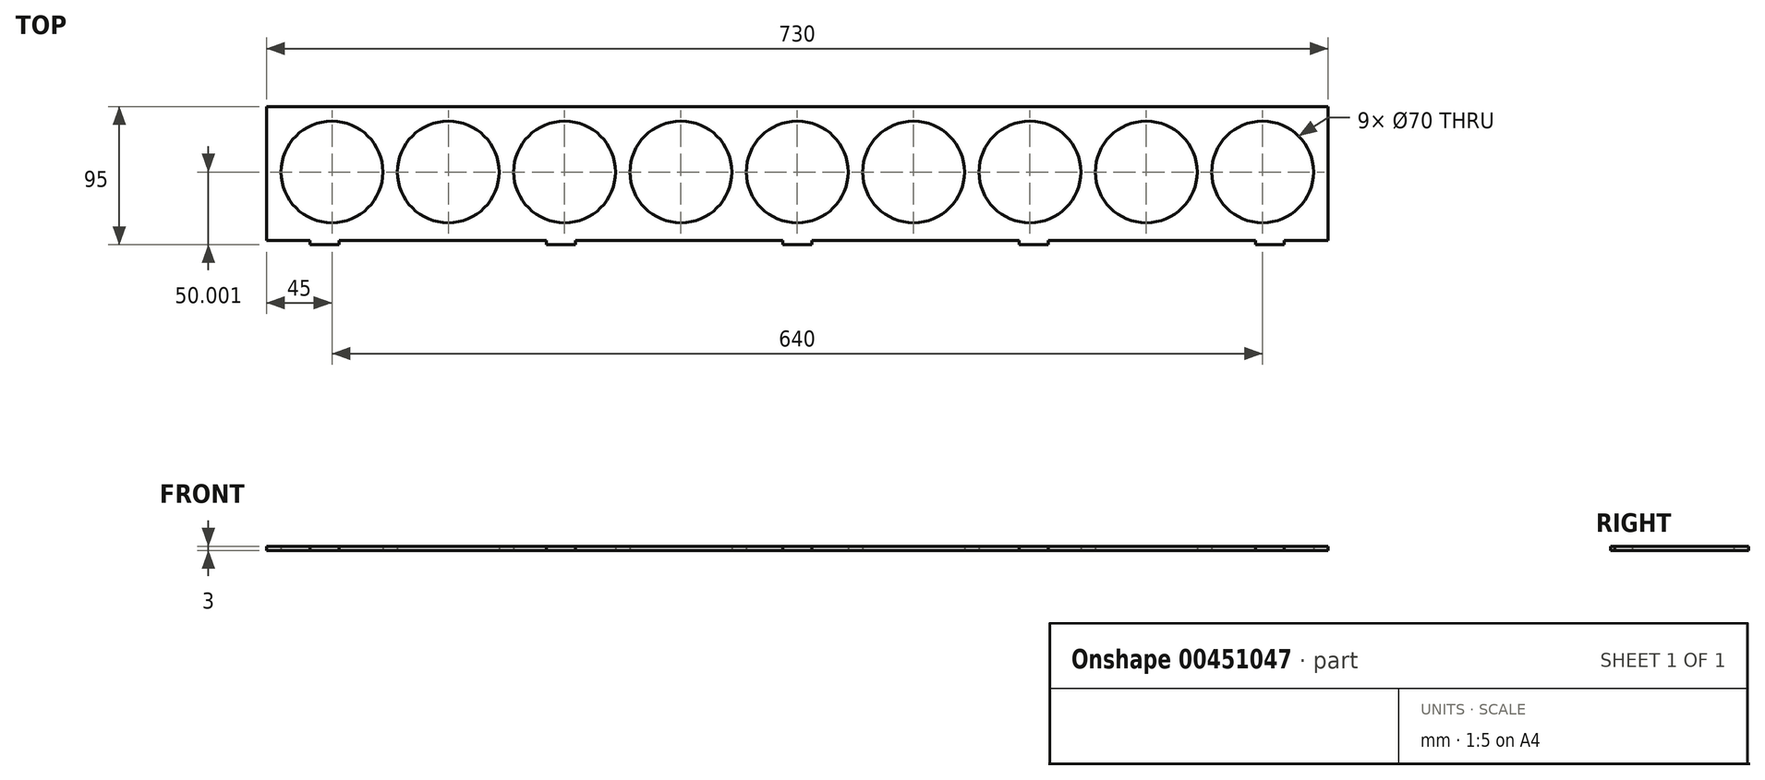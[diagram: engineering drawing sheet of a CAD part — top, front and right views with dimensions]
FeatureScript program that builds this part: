
annotation { "Feature Type Name" : "Feature", "Feature Type Description" : "" }
export const myFeature = defineFeature(function(context is Context, id is Id, definition is map)
    precondition{}
    {
        {
            var Q0;
            Q0=qCreatedBy(makeId("Top.planeOp"),FACE);
            var sketch = newSketch(context, id + "F0", { "sketchPlane" : qUnion([Q0])});
            skLineSegment(sketch, "E0.bottom", {"start": v(-365, 99.13) * mm, "end": v(365, 99.13) * mm});
            skLineSegment(sketch, "E0.left", {"start": v(-365, 99.13) * mm, "end": v(-365, 7.13) * mm});
            skLineSegment(sketch, "E0.right", {"start": v(365, 99.13) * mm, "end": v(365, 7.13) * mm});
            skCircle(sketch, "E1", {"center": v(-320, 54.13) * mm, "radius": 35 * mm});
            skCircle(sketch, "E2.1.0.0", {"center": v(-240, 54.13) * mm, "radius": 35 * mm});
            skCircle(sketch, "E2.2.0.0", {"center": v(-160, 54.13) * mm, "radius": 35 * mm});
            skCircle(sketch, "E2.3.0.0", {"center": v(-80, 54.13) * mm, "radius": 35 * mm});
            skCircle(sketch, "E2.4.0.0", {"center": v(0, 54.13) * mm, "radius": 35 * mm});
            skCircle(sketch, "E2.5.0.0", {"center": v(80, 54.13) * mm, "radius": 35 * mm});
            skCircle(sketch, "E2.6.0.0", {"center": v(160, 54.13) * mm, "radius": 35 * mm});
            skCircle(sketch, "E2.7.0.0", {"center": v(240, 54.13) * mm, "radius": 35 * mm});
            skCircle(sketch, "E2.8.0.0", {"center": v(320, 54.13) * mm, "radius": 35 * mm});
            skLineSegment(sketch, "E2.direction1", {"start": v(-320, 54.13) * mm, "end": v(-240, 54.13) * mm, "construction": true});
            skLineSegment(sketch, "E3", {"start": v(-365, 7.13) * mm, "end": v(-335, 7.13) * mm});
            skLineSegment(sketch, "E4", {"start": v(-335, 7.13) * mm, "end": v(-335, 4.13) * mm});
            skLineSegment(sketch, "E5", {"start": v(-335, 4.13) * mm, "end": v(-325, 4.13) * mm});
            skLineSegment(sketch, "E6.MirrorCS", {"start": v(-315, 4.13) * mm, "end": v(-325, 4.13) * mm});
            skLineSegment(sketch, "E7.MirrorCS", {"start": v(-315, 7.13) * mm, "end": v(-315, 4.13) * mm});
            skLineSegment(sketch, "E8", {"start": v(-162.5, 4.13) * mm, "end": v(-172.5, 4.13) * mm});
            skLineSegment(sketch, "E9", {"start": v(-172.5, 4.13) * mm, "end": v(-172.5, 7.13) * mm});
            skLineSegment(sketch, "E10", {"start": v(0, 4.13) * mm, "end": v(-10, 4.13) * mm});
            skLineSegment(sketch, "E11", {"start": v(-10, 4.13) * mm, "end": v(-10, 7.13) * mm});
            skLineSegment(sketch, "E12", {"start": v(162.5, 4.13) * mm, "end": v(152.5, 4.13) * mm});
            skLineSegment(sketch, "E13", {"start": v(152.5, 4.13) * mm, "end": v(152.5, 7.13) * mm});
            skLineSegment(sketch, "E14", {"start": v(325, 4.13) * mm, "end": v(315, 4.13) * mm});
            skLineSegment(sketch, "E15", {"start": v(315, 4.13) * mm, "end": v(315, 7.13) * mm});
            skLineSegment(sketch, "E16.MirrorCS", {"start": v(-152.5, 4.13) * mm, "end": v(-152.5, 7.13) * mm});
            skLineSegment(sketch, "E17.MirrorCS", {"start": v(-162.5, 4.13) * mm, "end": v(-152.5, 4.13) * mm});
            skLineSegment(sketch, "E18.MirrorCS", {"start": v(10, 4.13) * mm, "end": v(10, 7.13) * mm});
            skLineSegment(sketch, "E19.MirrorCS", {"start": v(0, 4.13) * mm, "end": v(10, 4.13) * mm});
            skLineSegment(sketch, "E20.MirrorCS", {"start": v(325, 4.13) * mm, "end": v(335, 4.13) * mm});
            skLineSegment(sketch, "E21.MirrorCS", {"start": v(335, 4.13) * mm, "end": v(335, 7.13) * mm});
            skLineSegment(sketch, "E22.MirrorCS", {"start": v(162.5, 4.13) * mm, "end": v(172.5, 4.13) * mm});
            skLineSegment(sketch, "E23.MirrorCS", {"start": v(172.5, 4.13) * mm, "end": v(172.5, 7.13) * mm});
            skLineSegment(sketch, "E24.trimOffspring", {"start": v(-315, 7.13) * mm, "end": v(-172.5, 7.13) * mm});
            skLineSegment(sketch, "E25.trimOffspring", {"start": v(-152.5, 7.13) * mm, "end": v(-10, 7.13) * mm});
            skLineSegment(sketch, "E26.trimOffspring", {"start": v(10, 7.13) * mm, "end": v(152.5, 7.13) * mm});
            skLineSegment(sketch, "E27.trimOffspring", {"start": v(335, 7.13) * mm, "end": v(365, 7.13) * mm});
            skLineSegment(sketch, "E28.trimOffspring", {"start": v(172.5, 7.13) * mm, "end": v(315, 7.13) * mm});
            skSolve(sketch);
        }
        {
            var Q0;
            Q0=qSketchRegion(id+"F0",true);
            extrude(context, id + "F1", {"entities" : qUnion([Q0]), "depth" : 3 * mm});
        }
    });
